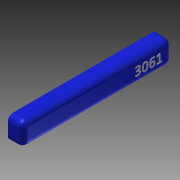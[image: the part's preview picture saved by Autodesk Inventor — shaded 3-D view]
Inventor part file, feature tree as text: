
AUTODESK INVENTOR PART (.ipt)
format: ipt  version: 2014 SP1 (Build 180222100, 222)  size: 364,032 bytes
history: native  units: in
note: dims shown in document units (in); Inventor stores cm internally (conversion verified against a paired STEP export)
features: reference x7, extrude x4, sketch x3, fillet x1, projected_geometry x1
ambient origin geometry x8: Origin, YZ Plane, XZ Plane, XY Plane, X Axis, Y Axis, Z Axis, Center Point
bodies: Solid1 (feature_tree)
feature tree (16):
  sketch  "Sketch1"  dims[d0=0.0625in d1=0.0in d3=1.0in]
  extrude  "Extrusion1"  Depth=1.0in
  extrude  "Extrusion2"  Depth=0.0625in
  extrude  "Extrusion3"  Depth=0.0625in TaperAngle=0.0deg
  fillet  "Fillet1"  Radius=1.3125in
  extrude  "Extrusion5"  Depth=0.0625in
  reference  "Reference4"
  reference  "Reference5"
  sketch  "Sketch2"  dims[d7=1.0in d9=0.0625in]
  reference  "Reference6"
  reference  "Reference7"
  reference  "Reference8"
  reference  "Reference9"
  reference  "Reference10"
  projected_geometry  "Projected Loop1"
  sketch  "Sketch4"  dims[d10=33.625in d11=0.0in d12=0.0625in d13=0.0in d14=1.3125in d20=0.0625in d21=0.0625in d26=1.0in d27=6.0in d28=2.5in d29=0.0625in d30=0.0in]
